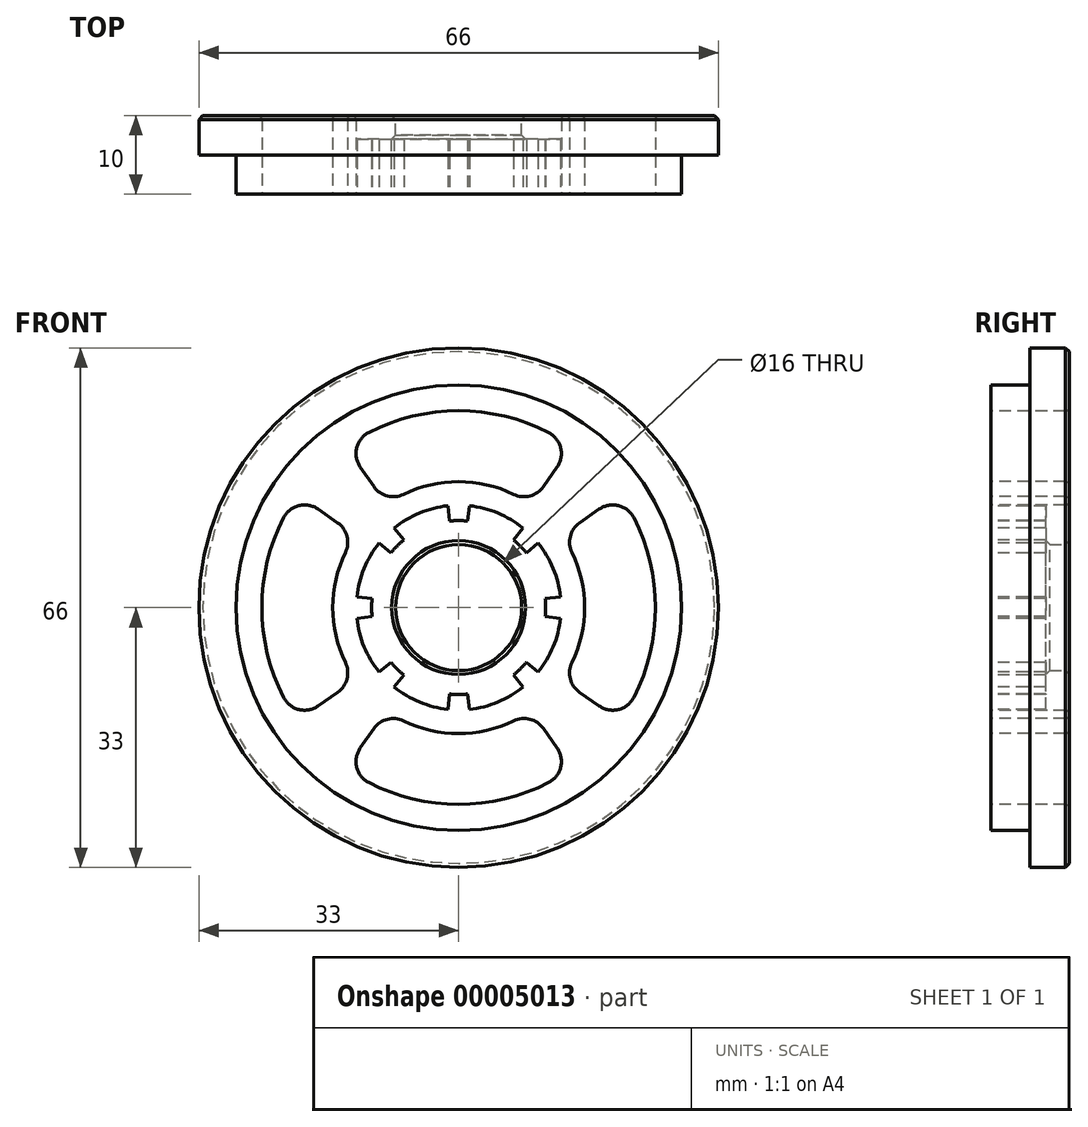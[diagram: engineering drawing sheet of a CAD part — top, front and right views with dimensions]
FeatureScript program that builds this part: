
annotation { "Feature Type Name" : "Feature", "Feature Type Description" : "" }
export const myFeature = defineFeature(function(context is Context, id is Id, definition is map)
    precondition{}
    {
        {
            var Q0;
            Q0=qCreatedBy(makeId("Front.planeOp"),FACE);
            var sketch = newSketch(context, id + "F0", { "sketchPlane" : qUnion([Q0])});
            skCircle(sketch, "E0", {"center": v(0, 0) * mm, "radius": 33 * mm});
            skCircle(sketch, "E1", {"center": v(0, 0) * mm, "radius": 8 * mm});
            skSolve(sketch);
        }
        {
            var Q0;
            Q0=makeQuery(id+"F0.imprint","IMPRINT",FACE,{"disambiguationData":[TD([[makeQuery(id+"F0.imprint","IMPRINT",EDGE,{"derivedFrom":sQuery(id+"F0.wireOp",EDGE,"E0")}),1.0]])]});
            extrude(context, id + "F1", {"entities" : qUnion([Q0]), "depth" : 10 * mm});
        }
        {
            var Q0;
            Q0=makeQuery(id+"F1.opExtrude","CAP_FACE",FACE,{"disambiguationData":[OSD([sQuery(id+"F0.wireOp",EDGE,"E0"),sQuery(id+"F0.wireOp",EDGE,"E1")])],"isStart":false});
            var sketch = newSketch(context, id + "F2", { "sketchPlane" : qUnion([Q0])});
            skCircle(sketch, "E2", {"center": v(0, 0) * mm, "radius": 33 * mm});
            skCircle(sketch, "E3", {"center": v(0, 0) * mm, "radius": 28.3 * mm});
            skSolve(sketch);
        }
        {
            var Q0;
            Q0=makeQuery(id+"F2.imprint","IMPRINT",FACE,{"disambiguationData":[TD([[makeQuery(id+"F2.imprint","IMPRINT",EDGE,{"derivedFrom":sQuery(id+"F2.wireOp",EDGE,"E2")}),1.0]])]});
            var Q1;
            Q1=makeQuery(id+"F1.opExtrude","CAP_FACE",FACE,{"disambiguationData":[OSD([sQuery(id+"F0.wireOp",EDGE,"E0"),sQuery(id+"F0.wireOp",EDGE,"E1")])],"isStart":true});
            extrude(context, id + "F3", {"entities" : qUnion([Q0, Q1]), "operationType" : NewBodyOperationType.REMOVE, "oppositeDirection" : true, "depth" : 5 * mm});
        }
        {
            var Q0;
            Q0=makeQuery(id+"F1.opExtrude","CAP_FACE",FACE,{"disambiguationData":[OSD([sQuery(id+"F0.wireOp",EDGE,"E0"),sQuery(id+"F0.wireOp",EDGE,"E1")])],"isStart":false});
            var sketch = newSketch(context, id + "F4", { "sketchPlane" : qUnion([Q0])});
            skCircle(sketch, "E4", {"center": v(0, 0) * mm, "radius": 11.05 * mm});
            skSolve(sketch);
        }
        {
            var Q0;
            Q0 = qSketchRegion(id + "F4", true);
            extrude(context, id + "F5", {"entities" : qUnion([Q0]), "operationType" : NewBodyOperationType.REMOVE, "oppositeDirection" : true, "depth" : 7 * mm});
        }
        {
            var Q0;
            Q0=makeQuery(id+"F1.opExtrude","CAP_FACE",FACE,{"disambiguationData":[OSD([sQuery(id+"F0.wireOp",EDGE,"E0"),sQuery(id+"F0.wireOp",EDGE,"E1")])],"isStart":false});
            var sketch = newSketch(context, id + "F6", { "sketchPlane" : qUnion([Q0])});
            skArc(sketch, "E5", {"start": v(-10.1, 8.18) * mm, "mid": v(-12.01, 4.97) * mm, "end": v(-12.93, 1.36) * mm});
            skLineSegment(sketch, "E6", {"start": v(0, 0) * mm, "end": v(-1.16, 10.99) * mm, "construction": true});
            skLineSegment(sketch, "E7", {"start": v(0, 0) * mm, "end": v(1.16, 10.99) * mm, "construction": true});
            skLineSegment(sketch, "E8", {"start": v(0, 0) * mm, "end": v(0, 13) * mm, "construction": true});
            skLineSegment(sketch, "E9", {"start": v(-1.16, 10.99) * mm, "end": v(-1.36, 12.93) * mm});
            skLineSegment(sketch, "E10", {"start": v(1.16, 10.99) * mm, "end": v(1.36, 12.93) * mm});
            skLineSegment(sketch, "E11.1.0", {"start": v(-8.59, 6.95) * mm, "end": v(-10.1, 8.18) * mm});
            skLineSegment(sketch, "E11.1.1", {"start": v(-6.95, 8.59) * mm, "end": v(-8.18, 10.1) * mm});
            skLineSegment(sketch, "E11.2.0", {"start": v(-10.99, -1.16) * mm, "end": v(-12.93, -1.36) * mm});
            skLineSegment(sketch, "E11.2.1", {"start": v(-10.99, 1.16) * mm, "end": v(-12.93, 1.36) * mm});
            skLineSegment(sketch, "E11.3.0", {"start": v(-6.95, -8.59) * mm, "end": v(-8.18, -10.1) * mm});
            skLineSegment(sketch, "E11.3.1", {"start": v(-8.59, -6.95) * mm, "end": v(-10.1, -8.18) * mm});
            skLineSegment(sketch, "E11.4.0", {"start": v(1.16, -10.99) * mm, "end": v(1.36, -12.93) * mm});
            skLineSegment(sketch, "E11.4.1", {"start": v(-1.16, -10.99) * mm, "end": v(-1.36, -12.93) * mm});
            skLineSegment(sketch, "E11.5.0", {"start": v(8.59, -6.95) * mm, "end": v(10.1, -8.18) * mm});
            skLineSegment(sketch, "E11.5.1", {"start": v(6.95, -8.59) * mm, "end": v(8.18, -10.1) * mm});
            skLineSegment(sketch, "E11.6.0", {"start": v(10.99, 1.16) * mm, "end": v(12.93, 1.36) * mm});
            skLineSegment(sketch, "E11.6.1", {"start": v(10.99, -1.16) * mm, "end": v(12.93, -1.36) * mm});
            skLineSegment(sketch, "E11.7.0", {"start": v(6.95, 8.59) * mm, "end": v(8.18, 10.1) * mm});
            skLineSegment(sketch, "E11.7.1", {"start": v(8.59, 6.95) * mm, "end": v(10.1, 8.18) * mm});
            skArc(sketch, "E12", {"start": v(-8.59, 6.95) * mm, "mid": v(-10.2, 4.23) * mm, "end": v(-10.99, 1.16) * mm});
            skArc(sketch, "E13.trimOffspring", {"start": v(-10.99, -1.16) * mm, "mid": v(-10.2, -4.23) * mm, "end": v(-8.59, -6.95) * mm});
            skArc(sketch, "E14.trimOffspring", {"start": v(-6.95, -8.59) * mm, "mid": v(-4.23, -10.2) * mm, "end": v(-1.16, -10.99) * mm});
            skArc(sketch, "E15.trimOffspring", {"start": v(1.16, -10.99) * mm, "mid": v(4.23, -10.2) * mm, "end": v(6.95, -8.59) * mm});
            skArc(sketch, "E16.trimOffspring", {"start": v(8.59, -6.95) * mm, "mid": v(10.2, -4.23) * mm, "end": v(10.99, -1.16) * mm});
            skArc(sketch, "E17.trimOffspring", {"start": v(10.99, 1.16) * mm, "mid": v(10.2, 4.23) * mm, "end": v(8.59, 6.95) * mm});
            skArc(sketch, "E18.trimOffspring", {"start": v(6.95, 8.59) * mm, "mid": v(4.23, 10.2) * mm, "end": v(1.16, 10.99) * mm});
            skArc(sketch, "E19.trimOffspring", {"start": v(-1.16, 10.99) * mm, "mid": v(-4.23, 10.2) * mm, "end": v(-6.95, 8.59) * mm});
            skArc(sketch, "E20.trimOffspring", {"start": v(-12.93, -1.36) * mm, "mid": v(-12.01, -4.97) * mm, "end": v(-10.1, -8.18) * mm});
            skArc(sketch, "E21.trimOffspring", {"start": v(8.18, 10.1) * mm, "mid": v(4.97, 12.01) * mm, "end": v(1.36, 12.93) * mm});
            skArc(sketch, "E22.trimOffspring", {"start": v(12.93, 1.36) * mm, "mid": v(12.01, 4.97) * mm, "end": v(10.1, 8.18) * mm});
            skArc(sketch, "E23.trimOffspring", {"start": v(-1.36, 12.93) * mm, "mid": v(-4.97, 12.01) * mm, "end": v(-8.18, 10.1) * mm});
            skArc(sketch, "E24.trimOffspring", {"start": v(-8.18, -10.1) * mm, "mid": v(-4.97, -12.01) * mm, "end": v(-1.36, -12.93) * mm});
            skArc(sketch, "E25.trimOffspring", {"start": v(1.36, -12.93) * mm, "mid": v(4.97, -12.01) * mm, "end": v(8.18, -10.1) * mm});
            skArc(sketch, "E26.trimOffspring", {"start": v(10.1, -8.18) * mm, "mid": v(12.01, -4.97) * mm, "end": v(12.93, -1.36) * mm});
            skSolve(sketch);
        }
        {
            var Q0;
            Q0 = qSketchRegion(id + "F6", true);
            var Q1;
            Q1=makeQuery(id+"F5.boolean.opBoolean","COPY",FACE,{"derivedFrom":makeQuery(id+"F5.opExtrude","CAP_FACE",FACE,{"disambiguationData":[OSD([sQuery(id+"F4.wireOp",EDGE,"E4")])],"isStart":false})});
            extrude(context, id + "F7", {"entities" : qUnion([Q0]), "operationType" : NewBodyOperationType.REMOVE, "endBound" : BoundingType.UP_TO_SURFACE, "oppositeDirection" : true, "endBoundEntityFace" : qUnion([Q1]), "depth" : 25 * mm});
        }
        {
            var Q0;
            Q0=makeQuery(id+"F3.boolean.opBoolean","COPY",EDGE,{"derivedFrom":makeQuery(id+"F3.opExtrude","CAP_EDGE",EDGE,{"disambiguationData":[OSD([sQuery(id+"F2.wireOp",EDGE,"E3")])],"isStart":true})});
            var Q1;
            {var subQ0=sQuery(id+"F4.wireOp",EDGE,"E4");Q1=makeQuery(id+"F7.boolean.opBoolean","SPLIT",EDGE,{"disambiguationData":[TD([makeQuery(id+"F7.opExtrude","SWEPT_FACE",FACE,{"disambiguationData":[OSD([sQuery(id+"F6.wireOp",EDGE,"E9")])]})])],"derivedFrom":makeQuery(id+"F5.boolean.opBoolean","COPY",EDGE,{"derivedFrom":makeQuery(id+"F5.opExtrude","CAP_EDGE",EDGE,{"disambiguationData":[OSD([subQ0])],"isStart":true})})});}
            var Q2;
            {var subQ0=sQuery(id+"F4.wireOp",EDGE,"E4");Q2=makeQuery(id+"F7.boolean.opBoolean","SPLIT",EDGE,{"disambiguationData":[TD([makeQuery(id+"F7.opExtrude","SWEPT_FACE",FACE,{"disambiguationData":[OSD([sQuery(id+"F6.wireOp",EDGE,"E11.7.0")])]})])],"derivedFrom":makeQuery(id+"F5.boolean.opBoolean","COPY",EDGE,{"derivedFrom":makeQuery(id+"F5.opExtrude","CAP_EDGE",EDGE,{"disambiguationData":[OSD([subQ0])],"isStart":true})})});}
            var Q3;
            {var subQ0=sQuery(id+"F4.wireOp",EDGE,"E4");Q3=makeQuery(id+"F7.boolean.opBoolean","SPLIT",EDGE,{"disambiguationData":[TD([makeQuery(id+"F7.opExtrude","SWEPT_FACE",FACE,{"disambiguationData":[OSD([sQuery(id+"F6.wireOp",EDGE,"E11.6.0")])]})])],"derivedFrom":makeQuery(id+"F5.boolean.opBoolean","COPY",EDGE,{"derivedFrom":makeQuery(id+"F5.opExtrude","CAP_EDGE",EDGE,{"disambiguationData":[OSD([subQ0])],"isStart":true})})});}
            var Q4;
            {var subQ0=sQuery(id+"F4.wireOp",EDGE,"E4");Q4=makeQuery(id+"F7.boolean.opBoolean","SPLIT",EDGE,{"disambiguationData":[TD([makeQuery(id+"F7.opExtrude","SWEPT_FACE",FACE,{"disambiguationData":[OSD([sQuery(id+"F6.wireOp",EDGE,"E11.5.0")])]})])],"derivedFrom":makeQuery(id+"F5.boolean.opBoolean","COPY",EDGE,{"derivedFrom":makeQuery(id+"F5.opExtrude","CAP_EDGE",EDGE,{"disambiguationData":[OSD([subQ0])],"isStart":true})})});}
            var Q5;
            {var subQ0=sQuery(id+"F4.wireOp",EDGE,"E4");Q5=makeQuery(id+"F7.boolean.opBoolean","SPLIT",EDGE,{"disambiguationData":[TD([makeQuery(id+"F7.opExtrude","SWEPT_FACE",FACE,{"disambiguationData":[OSD([sQuery(id+"F6.wireOp",EDGE,"E11.4.0")])]})])],"derivedFrom":makeQuery(id+"F5.boolean.opBoolean","COPY",EDGE,{"derivedFrom":makeQuery(id+"F5.opExtrude","CAP_EDGE",EDGE,{"disambiguationData":[OSD([subQ0])],"isStart":true})})});}
            var Q6;
            {var subQ0=sQuery(id+"F4.wireOp",EDGE,"E4");Q6=makeQuery(id+"F7.boolean.opBoolean","SPLIT",EDGE,{"disambiguationData":[TD([makeQuery(id+"F7.opExtrude","SWEPT_FACE",FACE,{"disambiguationData":[OSD([sQuery(id+"F6.wireOp",EDGE,"E11.3.0")])]})])],"derivedFrom":makeQuery(id+"F5.boolean.opBoolean","COPY",EDGE,{"derivedFrom":makeQuery(id+"F5.opExtrude","CAP_EDGE",EDGE,{"disambiguationData":[OSD([subQ0])],"isStart":true})})});}
            var Q7;
            {var subQ0=sQuery(id+"F4.wireOp",EDGE,"E4");Q7=makeQuery(id+"F7.boolean.opBoolean","SPLIT",EDGE,{"disambiguationData":[TD([makeQuery(id+"F7.opExtrude","SWEPT_FACE",FACE,{"disambiguationData":[OSD([sQuery(id+"F6.wireOp",EDGE,"E11.2.0")])]})])],"derivedFrom":makeQuery(id+"F5.boolean.opBoolean","COPY",EDGE,{"derivedFrom":makeQuery(id+"F5.opExtrude","CAP_EDGE",EDGE,{"disambiguationData":[OSD([subQ0])],"isStart":true})})});}
            var Q8;
            {var subQ0=sQuery(id+"F4.wireOp",EDGE,"E4");Q8=makeQuery(id+"F7.boolean.opBoolean","SPLIT",EDGE,{"disambiguationData":[TD([makeQuery(id+"F7.opExtrude","SWEPT_FACE",FACE,{"disambiguationData":[OSD([sQuery(id+"F6.wireOp",EDGE,"E11.1.0")])]})])],"derivedFrom":makeQuery(id+"F5.boolean.opBoolean","COPY",EDGE,{"derivedFrom":makeQuery(id+"F5.opExtrude","CAP_EDGE",EDGE,{"disambiguationData":[OSD([subQ0])],"isStart":true})})});}
            var Q9;
            Q9=makeQuery(id+"F3.boolean.opBoolean","COPY",EDGE,{"derivedFrom":makeQuery(id+"F3.opExtrude","CAP_EDGE",EDGE,{"disambiguationData":[OSD([sQuery(id+"F2.wireOp",EDGE,"E2")])],"isStart":false})});
            var Q10;
            Q10=makeQuery(id+"F1.opExtrude","CAP_EDGE",EDGE,{"disambiguationData":[OSD([sQuery(id+"F0.wireOp",EDGE,"E0")])],"isStart":true});
            var Q11;
            Q11=makeQuery(id+"F5.boolean.opBoolean","INTERSECT",EDGE,{"derivedFrom":[makeQuery(id+"F1.opExtrude","SWEPT_FACE",FACE,{"disambiguationData":[OSD([sQuery(id+"F0.wireOp",EDGE,"E1")])]}),makeQuery(id+"F5.opExtrude","CAP_FACE",FACE,{"disambiguationData":[OSD([sQuery(id+"F4.wireOp",EDGE,"E4")])],"isStart":false})]});
            var Q12;
            Q12=makeQuery(id+"F1.opExtrude","CAP_EDGE",EDGE,{"disambiguationData":[OSD([sQuery(id+"F0.wireOp",EDGE,"E1")])],"isStart":true});
            chamfer(context, id + "F8", {"entities" : qUnion([Q0, Q1, Q2, Q3, Q4, Q5, Q6, Q7, Q8, Q9, Q10, Q11, Q12]), "width" : .5 * mm, "tangentPropagation" : true});
        }
        {
            var Q0;
            Q0=makeQuery(id+"F1.opExtrude","CAP_FACE",FACE,{"disambiguationData":[OSD([sQuery(id+"F0.wireOp",EDGE,"E0"),sQuery(id+"F0.wireOp",EDGE,"E1")])],"isStart":false});
            var sketch = newSketch(context, id + "F9", { "sketchPlane" : qUnion([Q0])});
            skLineSegment(sketch, "E27", {"start": v(0, 0) * mm, "end": v(-9.18, 13.1) * mm, "construction": true});
            skArc(sketch, "E28", {"start": v(-20.48, 14.34) * mm, "mid": v(-25, 0) * mm, "end": v(-20.48, -14.34) * mm});
            skLineSegment(sketch, "E29", {"start": v(0, 0) * mm, "end": v(9.18, 13.1) * mm, "construction": true});
            skArc(sketch, "E30", {"start": v(-13.1, 9.18) * mm, "mid": v(-16, 0) * mm, "end": v(-13.1, -9.18) * mm});
            skLineSegment(sketch, "E31", {"start": v(-9.18, 13.1) * mm, "end": v(-14.34, 20.48) * mm});
            skLineSegment(sketch, "E32", {"start": v(9.18, 13.1) * mm, "end": v(14.34, 20.48) * mm});
            skLineSegment(sketch, "E33", {"start": v(0, 0) * mm, "end": v(0, 25) * mm, "construction": true});
            skLineSegment(sketch, "E34.1.0", {"start": v(-13.1, -9.18) * mm, "end": v(-20.48, -14.34) * mm});
            skLineSegment(sketch, "E34.1.1", {"start": v(-13.1, 9.18) * mm, "end": v(-20.48, 14.34) * mm});
            skLineSegment(sketch, "E34.2.0", {"start": v(9.18, -13.1) * mm, "end": v(14.34, -20.48) * mm});
            skLineSegment(sketch, "E34.2.1", {"start": v(-9.18, -13.1) * mm, "end": v(-14.34, -20.48) * mm});
            skLineSegment(sketch, "E34.3.0", {"start": v(13.1, 9.18) * mm, "end": v(20.48, 14.34) * mm});
            skLineSegment(sketch, "E34.3.1", {"start": v(13.1, -9.18) * mm, "end": v(20.48, -14.34) * mm});
            skArc(sketch, "E35.trimOffspring", {"start": v(9.18, 13.1) * mm, "mid": v(0, 16) * mm, "end": v(-9.18, 13.1) * mm});
            skArc(sketch, "E36.trimOffspring", {"start": v(14.34, 20.48) * mm, "mid": v(0, 25) * mm, "end": v(-14.34, 20.48) * mm});
            skArc(sketch, "E37.trimOffspring", {"start": v(13.1, -9.18) * mm, "mid": v(16, 0) * mm, "end": v(13.1, 9.18) * mm});
            skArc(sketch, "E38.trimOffspring", {"start": v(20.48, -14.34) * mm, "mid": v(25, 0) * mm, "end": v(20.48, 14.34) * mm});
            skArc(sketch, "E39.trimOffspring", {"start": v(-14.34, -20.48) * mm, "mid": v(0, -25) * mm, "end": v(14.34, -20.48) * mm});
            skArc(sketch, "E40.trimOffspring", {"start": v(-9.18, -13.1) * mm, "mid": v(0, -16) * mm, "end": v(9.18, -13.1) * mm});
            skSolve(sketch);
        }
        {
            var Q0;
            Q0 = qSketchRegion(id + "F9", true);
            extrude(context, id + "F10", {"entities" : qUnion([Q0]), "operationType" : NewBodyOperationType.REMOVE, "endBound" : BoundingType.THROUGH_ALL, "oppositeDirection" : true, "depth" : 25 * mm});
        }
        {
            var Q0;
            Q0=makeQuery(id+"F10.boolean.opBoolean","COPY",EDGE,{"derivedFrom":makeQuery(id+"F10.opExtrude","SWEPT_EDGE",EDGE,{"disambiguationData":[OSD([sQuery(id+"F9.wireOp",EDGE,"E31"),sQuery(id+"F9.wireOp",EDGE,"E36.trimOffspring")])]})});
            var Q1;
            Q1=makeQuery(id+"F10.boolean.opBoolean","COPY",EDGE,{"derivedFrom":makeQuery(id+"F10.opExtrude","SWEPT_EDGE",EDGE,{"disambiguationData":[OSD([sQuery(id+"F9.wireOp",EDGE,"E34.3.0"),sQuery(id+"F9.wireOp",EDGE,"E37.trimOffspring")])]})});
            var Q2;
            Q2=makeQuery(id+"F10.boolean.opBoolean","COPY",EDGE,{"derivedFrom":makeQuery(id+"F10.opExtrude","SWEPT_EDGE",EDGE,{"disambiguationData":[OSD([sQuery(id+"F9.wireOp",EDGE,"E34.3.1"),sQuery(id+"F9.wireOp",EDGE,"E37.trimOffspring")])]})});
            var Q3;
            Q3=makeQuery(id+"F10.boolean.opBoolean","COPY",EDGE,{"derivedFrom":makeQuery(id+"F10.opExtrude","SWEPT_EDGE",EDGE,{"disambiguationData":[OSD([sQuery(id+"F9.wireOp",EDGE,"E34.2.1"),sQuery(id+"F9.wireOp",EDGE,"E39.trimOffspring")])]})});
            var Q4;
            Q4=makeQuery(id+"F10.boolean.opBoolean","COPY",EDGE,{"derivedFrom":makeQuery(id+"F10.opExtrude","SWEPT_EDGE",EDGE,{"disambiguationData":[OSD([sQuery(id+"F9.wireOp",EDGE,"E34.3.1"),sQuery(id+"F9.wireOp",EDGE,"E38.trimOffspring")])]})});
            var Q5;
            Q5=makeQuery(id+"F10.boolean.opBoolean","COPY",EDGE,{"derivedFrom":makeQuery(id+"F10.opExtrude","SWEPT_EDGE",EDGE,{"disambiguationData":[OSD([sQuery(id+"F9.wireOp",EDGE,"E34.3.0"),sQuery(id+"F9.wireOp",EDGE,"E38.trimOffspring")])]})});
            var Q6;
            Q6=makeQuery(id+"F10.boolean.opBoolean","COPY",EDGE,{"derivedFrom":makeQuery(id+"F10.opExtrude","SWEPT_EDGE",EDGE,{"disambiguationData":[OSD([sQuery(id+"F9.wireOp",EDGE,"E34.2.0"),sQuery(id+"F9.wireOp",EDGE,"E40.trimOffspring")])]})});
            var Q7;
            Q7=makeQuery(id+"F10.boolean.opBoolean","COPY",EDGE,{"derivedFrom":makeQuery(id+"F10.opExtrude","SWEPT_EDGE",EDGE,{"disambiguationData":[OSD([sQuery(id+"F9.wireOp",EDGE,"E34.2.1"),sQuery(id+"F9.wireOp",EDGE,"E40.trimOffspring")])]})});
            var Q8;
            Q8=makeQuery(id+"F10.boolean.opBoolean","COPY",EDGE,{"derivedFrom":makeQuery(id+"F10.opExtrude","SWEPT_EDGE",EDGE,{"disambiguationData":[OSD([sQuery(id+"F9.wireOp",EDGE,"E28"),sQuery(id+"F9.wireOp",EDGE,"E34.1.1")])]})});
            var Q9;
            Q9=makeQuery(id+"F10.boolean.opBoolean","COPY",EDGE,{"derivedFrom":makeQuery(id+"F10.opExtrude","SWEPT_EDGE",EDGE,{"disambiguationData":[OSD([sQuery(id+"F9.wireOp",EDGE,"E34.2.0"),sQuery(id+"F9.wireOp",EDGE,"E39.trimOffspring")])]})});
            var Q10;
            Q10=makeQuery(id+"F10.boolean.opBoolean","COPY",EDGE,{"derivedFrom":makeQuery(id+"F10.opExtrude","SWEPT_EDGE",EDGE,{"disambiguationData":[OSD([sQuery(id+"F9.wireOp",EDGE,"E32"),sQuery(id+"F9.wireOp",EDGE,"E36.trimOffspring")])]})});
            var Q11;
            Q11=makeQuery(id+"F10.boolean.opBoolean","COPY",EDGE,{"derivedFrom":makeQuery(id+"F10.opExtrude","SWEPT_EDGE",EDGE,{"disambiguationData":[OSD([sQuery(id+"F9.wireOp",EDGE,"E32"),sQuery(id+"F9.wireOp",EDGE,"E35.trimOffspring")])]})});
            var Q12;
            Q12=makeQuery(id+"F10.boolean.opBoolean","COPY",EDGE,{"derivedFrom":makeQuery(id+"F10.opExtrude","SWEPT_EDGE",EDGE,{"disambiguationData":[OSD([sQuery(id+"F9.wireOp",EDGE,"E28"),sQuery(id+"F9.wireOp",EDGE,"E34.1.0")])]})});
            var Q13;
            Q13=makeQuery(id+"F10.boolean.opBoolean","COPY",EDGE,{"derivedFrom":makeQuery(id+"F10.opExtrude","SWEPT_EDGE",EDGE,{"disambiguationData":[OSD([sQuery(id+"F9.wireOp",EDGE,"E30"),sQuery(id+"F9.wireOp",EDGE,"E34.1.0")])]})});
            var Q14;
            Q14=makeQuery(id+"F10.boolean.opBoolean","COPY",EDGE,{"derivedFrom":makeQuery(id+"F10.opExtrude","SWEPT_EDGE",EDGE,{"disambiguationData":[OSD([sQuery(id+"F9.wireOp",EDGE,"E30"),sQuery(id+"F9.wireOp",EDGE,"E34.1.1")])]})});
            var Q15;
            Q15=makeQuery(id+"F10.boolean.opBoolean","COPY",EDGE,{"derivedFrom":makeQuery(id+"F10.opExtrude","SWEPT_EDGE",EDGE,{"disambiguationData":[OSD([sQuery(id+"F9.wireOp",EDGE,"E31"),sQuery(id+"F9.wireOp",EDGE,"E35.trimOffspring")])]})});
            fillet(context, id + "F11", {"entities" : qUnion([Q0, Q1, Q2, Q3, Q4, Q5, Q6, Q7, Q8, Q9, Q10, Q11, Q12, Q13, Q14, Q15]), "radius" : 3 * mm, "tangentPropagation" : true, "allowEdgeOverflow" : false});
        }
        {
            var Q0;
            Q0=makeQuery(id+"F10.boolean.opBoolean","INTERSECT",EDGE,{"derivedFrom":[makeQuery(id+"F1.opExtrude","CAP_FACE",FACE,{"disambiguationData":[OSD([sQuery(id+"F0.wireOp",EDGE,"E0"),sQuery(id+"F0.wireOp",EDGE,"E1")])],"isStart":true}),makeQuery(id+"F10.opExtrude","SWEPT_FACE",FACE,{"disambiguationData":[OSD([sQuery(id+"F9.wireOp",EDGE,"E28")])]})]});
            var Q1;
            Q1=makeQuery(id+"F10.boolean.opBoolean","INTERSECT",EDGE,{"derivedFrom":[makeQuery(id+"F1.opExtrude","CAP_FACE",FACE,{"disambiguationData":[OSD([sQuery(id+"F0.wireOp",EDGE,"E0"),sQuery(id+"F0.wireOp",EDGE,"E1")])],"isStart":true}),makeQuery(id+"F10.opExtrude","SWEPT_FACE",FACE,{"disambiguationData":[OSD([sQuery(id+"F9.wireOp",EDGE,"E36.trimOffspring")])]})]});
            var Q2;
            Q2=makeQuery(id+"F10.boolean.opBoolean","INTERSECT",EDGE,{"derivedFrom":[makeQuery(id+"F1.opExtrude","CAP_FACE",FACE,{"disambiguationData":[OSD([sQuery(id+"F0.wireOp",EDGE,"E0"),sQuery(id+"F0.wireOp",EDGE,"E1")])],"isStart":true}),makeQuery(id+"F10.opExtrude","SWEPT_FACE",FACE,{"disambiguationData":[OSD([sQuery(id+"F9.wireOp",EDGE,"E37.trimOffspring")])]})]});
            var Q3;
            Q3=makeQuery(id+"F10.boolean.opBoolean","INTERSECT",EDGE,{"derivedFrom":[makeQuery(id+"F1.opExtrude","CAP_FACE",FACE,{"disambiguationData":[OSD([sQuery(id+"F0.wireOp",EDGE,"E0"),sQuery(id+"F0.wireOp",EDGE,"E1")])],"isStart":true}),makeQuery(id+"F10.opExtrude","SWEPT_FACE",FACE,{"disambiguationData":[OSD([sQuery(id+"F9.wireOp",EDGE,"E40.trimOffspring")])]})]});
            var Q4;
            Q4=makeQuery(id+"F10.boolean.opBoolean","COPY",EDGE,{"derivedFrom":makeQuery(id+"F10.opExtrude","CAP_EDGE",EDGE,{"disambiguationData":[OSD([sQuery(id+"F9.wireOp",EDGE,"E28")])],"isStart":true})});
            var Q5;
            Q5=makeQuery(id+"F10.boolean.opBoolean","COPY",EDGE,{"derivedFrom":makeQuery(id+"F10.opExtrude","CAP_EDGE",EDGE,{"disambiguationData":[OSD([sQuery(id+"F9.wireOp",EDGE,"E36.trimOffspring")])],"isStart":true})});
            var Q6;
            Q6=makeQuery(id+"F10.boolean.opBoolean","COPY",EDGE,{"derivedFrom":makeQuery(id+"F10.opExtrude","CAP_EDGE",EDGE,{"disambiguationData":[OSD([sQuery(id+"F9.wireOp",EDGE,"E38.trimOffspring")])],"isStart":true})});
            var Q7;
            Q7=makeQuery(id+"F10.boolean.opBoolean","COPY",EDGE,{"derivedFrom":makeQuery(id+"F10.opExtrude","CAP_EDGE",EDGE,{"disambiguationData":[OSD([sQuery(id+"F9.wireOp",EDGE,"E39.trimOffspring")])],"isStart":true})});
            fillet(context, id + "F12", {"entities" : qUnion([Q0, Q1, Q2, Q3, Q4, Q5, Q6, Q7]), "radius" : .5 * mm, "tangentPropagation" : true, "allowEdgeOverflow" : false});
        }
    });
